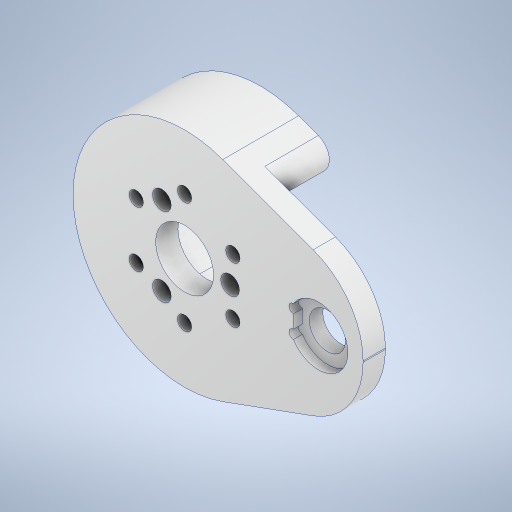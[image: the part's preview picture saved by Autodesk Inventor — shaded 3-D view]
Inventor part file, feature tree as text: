
AUTODESK INVENTOR PART (.ipt)
format: ipt  version: 2024.3 (Build 283343000, 343)  size: 539,648 bytes
history: native  units: mm
features: sketch x10, extrude x6, hole x4, other x2, fillet x2, mirror x1
ambient origin geometry x8: Origin, YZ Plane, XZ Plane, XY Plane, X Axis, Y Axis, Z Axis, Center Point
bodies: Body1 (feature_tree)
feature tree (25):
  other  "ソリッド1"
  other  "作業平面1"
  extrude  "押し出し9"  Depth=50.0mm
  extrude  "押し出し10"  Depth=8.1mm
  extrude  "押し出し11"  Depth=30.0mm
  hole  "穴5"  [1 undecoded]
  hole  "穴6"  [1 undecoded]
  extrude  "押し出し12"  Depth=25.0mm
  hole  "穴7"  [1 undecoded]
  fillet  "フィレット9"  Radius=5.0mm
  hole  "穴8"  [1 undecoded]
  fillet  "フィレット12"  Radius=2.0mm
  mirror  "ミラー1"
  extrude  "押し出し13"  Depth=34.0mm
  extrude  "押し出し14"  Depth=3.490659mm
  sketch  "スケッチ14"
  sketch  "スケッチ15"
  sketch  "スケッチ16"
  sketch  "スケッチ17"
  sketch  "スケッチ18"
  sketch  "スケッチ19"
  sketch  "スケッチ20"
  sketch  "スケッチ21"
  sketch  "スケッチ22"
  sketch  "スケッチ23"
note: 4 required parameter values undecoded (feature->parameter linkage not recoverable at this tier; creation-order binding heuristic only, values carry confidence <= 0.55)
